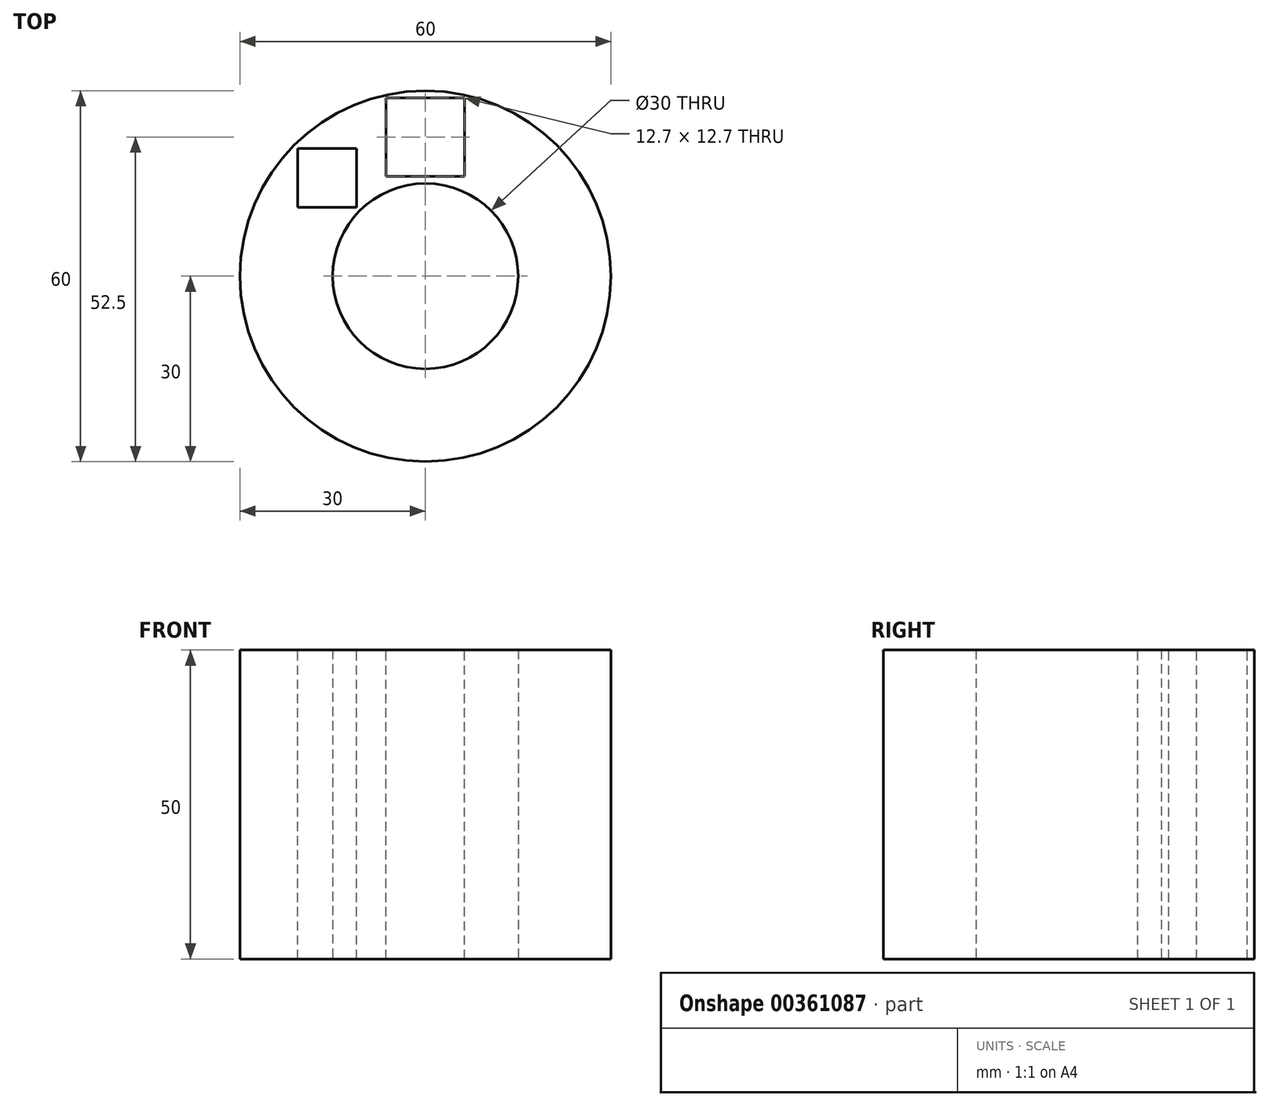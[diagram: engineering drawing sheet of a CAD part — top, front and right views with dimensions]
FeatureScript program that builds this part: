
annotation { "Feature Type Name" : "Feature", "Feature Type Description" : "" }
export const myFeature = defineFeature(function(context is Context, id is Id, definition is map)
    precondition{}
    {
        {
            var Q0;
            Q0=qCreatedBy(makeId("Top.planeOp"),FACE);
            var sketch = newSketch(context, id + "F0", { "sketchPlane" : qUnion([Q0])});
            skCircle(sketch, "E0", {"center": v(0, 0) * mm, "radius": 15 * mm});
            skCircle(sketch, "E1", {"center": v(0, 0) * mm, "radius": 30 * mm});
            skSolve(sketch);
        }
        {
            var Q0;
            Q0=makeQuery(id+"F0.imprint","IMPRINT",FACE,{"disambiguationData":[TD([[makeQuery(id+"F0.imprint","IMPRINT",EDGE,{"derivedFrom":sQuery(id+"F0.wireOp",EDGE,"E0")}),-1.0]])]});
            extrude(context, id + "F1", {"entities" : qUnion([Q0]), "depth" : 50 * mm});
        }
        {
            var Q0;
            Q0=makeQuery(id+"F1.opExtrude","CAP_FACE",FACE,{"disambiguationData":[OSD([sQuery(id+"F0.wireOp",EDGE,"E0"),sQuery(id+"F0.wireOp",EDGE,"E1")])],"isStart":false});
            var sketch = newSketch(context, id + "F2", { "sketchPlane" : qUnion([Q0])});
            skCircle(sketch, "E2", {"center": v(0, 0) * mm, "radius": 22.5 * mm, "construction": true});
            skLineSegment(sketch, "E3", {"start": v(0, 30) * mm, "end": v(0, 15) * mm, "construction": true});
            skPoint(sketch, "E4", {"position": v(0, 22.5) * mm});
            skLineSegment(sketch, "E5.bottom", {"start": v(6.35, 28.85) * mm, "end": v(-6.35, 28.85) * mm});
            skLineSegment(sketch, "E5.top", {"start": v(6.35, 16.15) * mm, "end": v(-6.35, 16.15) * mm});
            skLineSegment(sketch, "E5.left", {"start": v(6.35, 28.85) * mm, "end": v(6.35, 16.15) * mm});
            skLineSegment(sketch, "E5.right", {"start": v(-6.35, 28.85) * mm, "end": v(-6.35, 16.15) * mm});
            skSolve(sketch);
        }
        {
            var Q0;
            Q0 = qSketchRegion(id + "F2", true);
            extrude(context, id + "F3", {"entities" : qUnion([Q0]), "operationType" : NewBodyOperationType.REMOVE, "endBound" : BoundingType.THROUGH_ALL, "oppositeDirection" : true, "depth" : 25 * mm});
        }
        {
            var Q0;
            Q0=makeQuery(id+"F1.opExtrude","CAP_FACE",FACE,{"disambiguationData":[OSD([sQuery(id+"F0.wireOp",EDGE,"E0"),sQuery(id+"F0.wireOp",EDGE,"E1")])],"isStart":false});
            var sketch = newSketch(context, id + "F4", { "sketchPlane" : qUnion([Q0])});
            skCircle(sketch, "E6", {"center": v(0, 0) * mm, "radius": 22.5 * mm, "construction": true});
            skLineSegment(sketch, "E7", {"start": v(0, 15) * mm, "end": v(0, 30) * mm, "construction": true});
            skPoint(sketch, "E7.endSnap0", {"position": v(0, 28.85) * mm});
            skPoint(sketch, "E8", {"position": v(0, 22.5) * mm});
            skLineSegment(sketch, "E9.bottom", {"start": v(-11.15, 11.15) * mm, "end": v(-20.67, 11.15) * mm});
            skLineSegment(sketch, "E9.top", {"start": v(-11.15, 20.67) * mm, "end": v(-20.67, 20.67) * mm});
            skLineSegment(sketch, "E9.left", {"start": v(-11.15, 11.15) * mm, "end": v(-11.15, 20.67) * mm});
            skLineSegment(sketch, "E9.right", {"start": v(-20.67, 11.15) * mm, "end": v(-20.67, 20.67) * mm});
            skPoint(sketch, "E9.middle", {"position": v(-15.9, 15.9) * mm});
            skLineSegment(sketch, "E10", {"start": v(-15.9, 15.9) * mm, "end": v(0, 0) * mm, "construction": true});
            skSolve(sketch);
        }
        {
            var Q0;
            Q0=makeQuery(id+"F4.imprint","IMPRINT",FACE,{"disambiguationData":[TD([[makeQuery(id+"F4.imprint","IMPRINT",EDGE,{"derivedFrom":sQuery(id+"F4.wireOp",EDGE,"E9.bottom")}),-1.0]])]});
            extrude(context, id + "F5", {"entities" : qUnion([Q0]), "operationType" : NewBodyOperationType.REMOVE, "endBound" : BoundingType.THROUGH_ALL, "oppositeDirection" : true, "depth" : 25 * mm});
        }
    });
